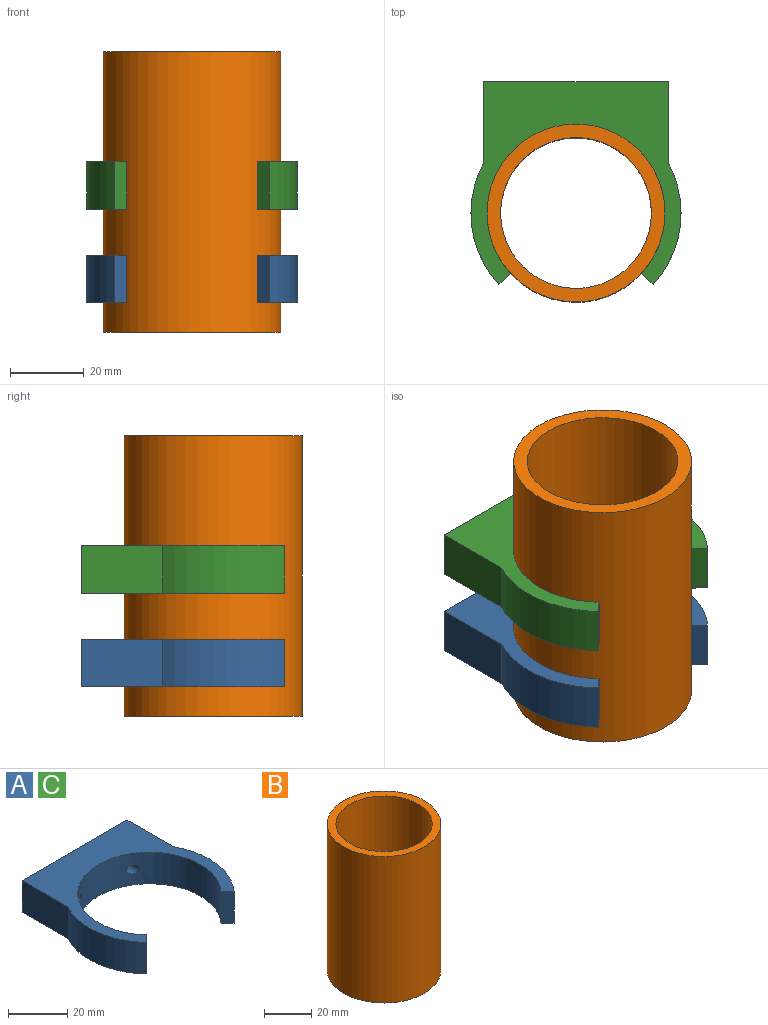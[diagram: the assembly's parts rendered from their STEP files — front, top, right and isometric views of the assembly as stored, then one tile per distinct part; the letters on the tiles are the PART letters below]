
ASSEMBLY  parts=3 mates=2
PART A: 12 faces, bbox 57x55x13 mm
  f0: cylinder r=24.13mm len=48.26mm, axis (0,0,-1), area 1424mm2, adj f3,f4,f8,f9,f10,f11
  f1: plane 50x13mm, normal (0,1,0), area 624.9mm2, adj f6,f7,f8,f9,f10,f11
  f2: cylinder r=28.5mm len=33.03mm, axis (0,0,-1), area 462mm2, adj f3,f7,f8,f9
  f3: plane 13x3.21mm, normal (0.68,-0.73,0), area 56.8mm2, adj f0,f2,f8,f9
  f4: plane 13x3.21mm, normal (-0.68,-0.73,0), area 56.8mm2, adj f0,f5,f8,f9
  f5: cylinder r=28.5mm len=33.03mm, axis (0,0,-1), area 462mm2, adj f4,f6,f8,f9
  f6: plane 22x13mm, normal (1,0,0), area 286mm2, adj f1,f5,f8,f9
  f7: plane 22x13mm, normal (-1,0,0), area 286mm2, adj f1,f2,f8,f9
  f8: plane 57x55.03mm, normal (0,0,1), area 1105.9mm2, adj f0,f1,f2,f3,f4,f5,f6,f7
  f9: plane 57x55.03mm, normal (0,0,-1), area 1105.9mm2, adj f0,f1,f2,f3,f4,f5,f6,f7
  f10: cylinder r=2mm len=16.55mm, axis (0,1,0), area 191.4mm2, adj f0,f1
  f11: cylinder r=2mm len=16.55mm, axis (0,1,0), area 191.4mm2, adj f0,f1
PART B: 4 faces, bbox 48.3x48.3x76.2 mm
  f0: cylinder r=20.45mm len=76.2mm, axis (0,0,-1), area 9789.6mm2, adj f2,f3
  f1: cylinder r=24.13mm len=76.2mm, axis (0,0,-1), area 11552.9mm2, adj f2,f3
  f2: plane 48.26x48.26mm, normal (0,0,1), area 515.8mm2, adj f0,f1
  f3: plane 48.26x48.26mm, normal (0,0,-1), area 515.8mm2, adj f0,f1
PART C: same geometry as A
PLACE A t=(-7.37,-9.51,64.77)mm
PLACE B t=(-7.37,-9.51,56.77)mm
PLACE C t=(-7.37,-9.51,90.17)mm
MATE fastened C.f0 <-> A.f0  axis (0,0,1) through (-7.37,-9.51,103.17)mm
MATE fastened A.f0 <-> B.f1  axis (0,0,-1) through (-7.37,-9.51,64.77)mm
